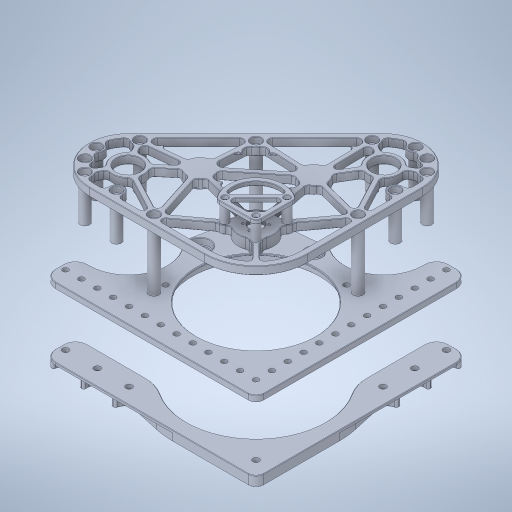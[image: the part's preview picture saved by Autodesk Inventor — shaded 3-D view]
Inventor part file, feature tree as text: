
AUTODESK INVENTOR PART (.ipt)
format: ipt  version: 2023.3 (Build 273359000, 359)  size: 1,677,312 bytes
history: native  units: in
note: dims shown in document units (in); Inventor stores cm internally (conversion verified against a paired STEP export)
features: other x14, chamfer x4
ambient origin geometry x8: Origin, YZ Plane, XZ Plane, XY Plane, X Axis, Y Axis, Z Axis, Center Point
bodies: Solid1 (feature_tree), Solid2 (feature_tree), Solid3 (feature_tree), Solid4 (feature_tree), Solid5 (feature_tree), Solid6 (feature_tree), Solid7 (feature_tree), Solid8 (feature_tree), Solid9 (feature_tree), Solid10 (feature_tree), Solid11 (feature_tree), Solid13 (feature_tree), Solid14 (feature_tree), Solid15 (feature_tree), Solid16 (feature_tree), Solid17 (feature_tree), Solid18 (feature_tree), Solid19 (feature_tree)
feature tree (18):
  other  "Boss-Extrude4[1]"
  other  "Boss-Extrude4[2]"
  other  "Boss-Extrude4[3]"
  other  "Boss-Extrude6[1]"
  other  "Boss-Extrude6[2]"
  other  "Boss-Extrude6[3]"
  other  "Boss-Extrude6[4]"
  other  "Boss-Extrude6[5]"
  other  "Boss-Extrude6[6]"
  other  "Boss-Extrude6[7]"
  other  "Boss-Extrude6[8]"
  other  "Boss-Extrude17[1]"
  other  "Boss-Extrude17[2]"
  other  "Boss-Extrude17[3]"
  chamfer  "Chamfer4"  [1 undecoded]
  chamfer  "Chamfer1"  [1 undecoded]
  chamfer  "Chamfer3"  [1 undecoded]
  chamfer  "Chamfer2"  [1 undecoded]
note: 4 required parameter values undecoded (feature->parameter linkage not recoverable at this tier; creation-order binding heuristic only, values carry confidence <= 0.55)
